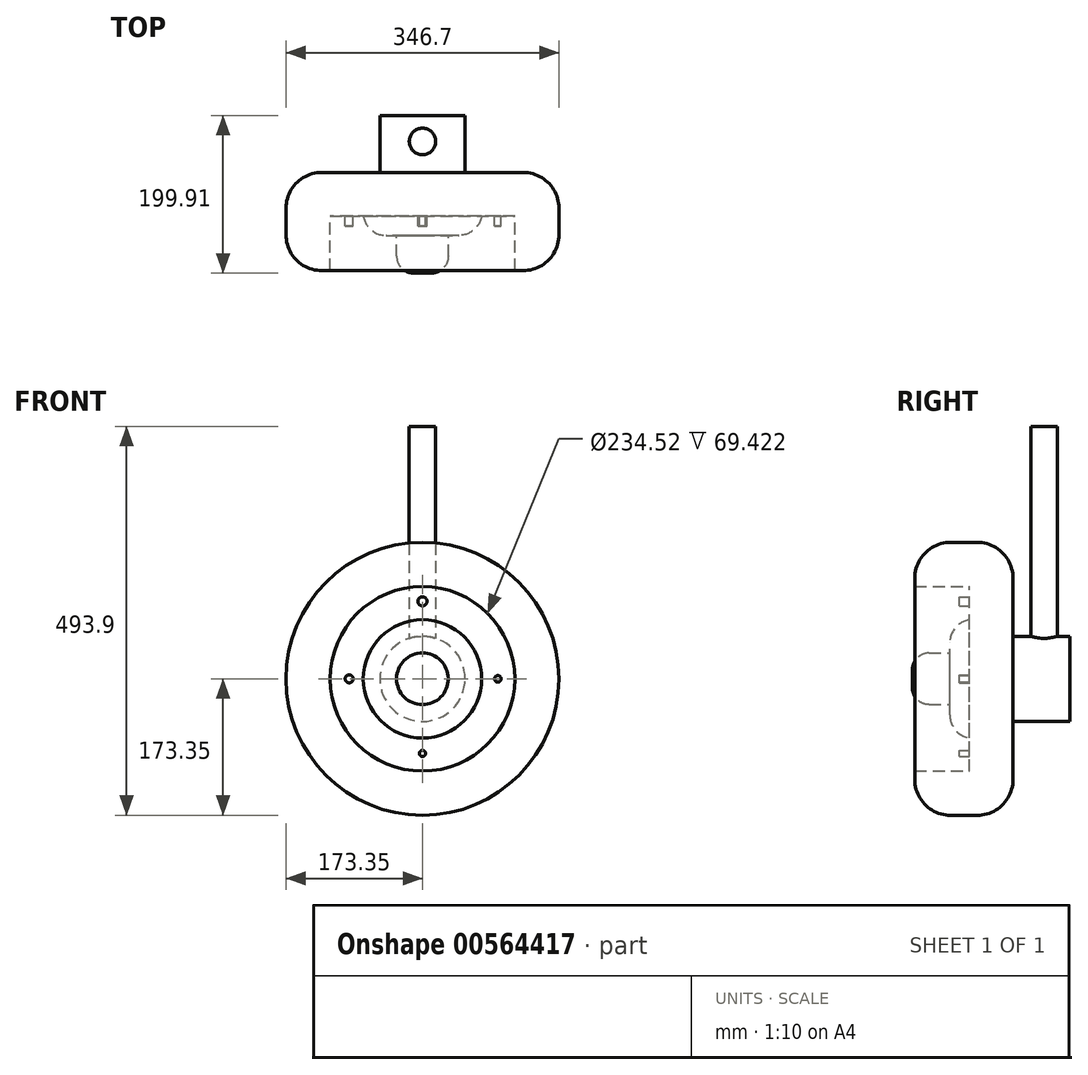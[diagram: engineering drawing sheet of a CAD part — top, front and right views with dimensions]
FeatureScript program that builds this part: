
annotation { "Feature Type Name" : "Feature", "Feature Type Description" : "" }
export const myFeature = defineFeature(function(context is Context, id is Id, definition is map)
    precondition{}
    {
        {
            var Q0;
            Q0=qCreatedBy(makeId("Front.planeOp"),FACE);
            var sketch = newSketch(context, id + "F0", { "sketchPlane" : qUnion([Q0])});
            skCircle(sketch, "E0", {"center": v(0, 0) * mm, "radius": 173.35 * mm});
            skCircle(sketch, "E1", {"center": v(0, 0) * mm, "radius": 117.26 * mm});
            skCircle(sketch, "E2", {"center": v(0, 0) * mm, "radius": 25.29 * mm});
            skSolve(sketch);
        }
        {
            var Q0;
            Q0=makeQuery(id+"F0.imprint","IMPRINT",FACE,{"disambiguationData":[TD([[makeQuery(id+"F0.imprint","IMPRINT",EDGE,{"derivedFrom":sQuery(id+"F0.wireOp",EDGE,"E0")}),1.0]])]});
            extrude(context, id + "F1", {"entities" : qUnion([Q0]), "depth" : 124.69 * mm, "offsetDistance" : 25.4 * mm});
        }
        {
            var Q0;
            Q0=makeQuery(id+"F1.opExtrude","CAP_EDGE",EDGE,{"disambiguationData":[OSD([sQuery(id+"F0.wireOp",EDGE,"E0")])],"isStart":true});
            var Q1;
            Q1=makeQuery(id+"F1.opExtrude","CAP_EDGE",EDGE,{"disambiguationData":[OSD([sQuery(id+"F0.wireOp",EDGE,"E0")])],"isStart":false});
            fillet(context, id + "F2", {"entities" : qUnion([Q0, Q1]), "radius" : 45.43 * mm, "tangentPropagation" : true, "allowEdgeOverflow" : false});
        }
        {
            var Q0;
            Q0=qCreatedBy(makeId("Front.planeOp"),FACE);
            var sketch = newSketch(context, id + "F3", { "sketchPlane" : qUnion([Q0])});
            skCircle(sketch, "E3", {"center": v(0, 0) * mm, "radius": 121.25 * mm});
            skSolve(sketch);
        }
        {
            var Q0;
            Q0 = qSketchRegion(id + "F3", true);
            extrude(context, id + "F4", {"entities" : qUnion([Q0]), "operationType" : NewBodyOperationType.ADD, "depth" : 55.27 * mm, "offsetDistance" : 25.4 * mm});
        }
        {
            var Q0;
            Q0=qCreatedBy(makeId("Front.planeOp"),FACE);
            var sketch = newSketch(context, id + "F5", { "sketchPlane" : qUnion([Q0])});
            skCircle(sketch, "E4", {"center": v(0, 0) * mm, "radius": 75.17 * mm});
            skSolve(sketch);
        }
        {
            var Q0;
            Q0 = qSketchRegion(id + "F5", true);
            extrude(context, id + "F6", {"entities" : qUnion([Q0]), "operationType" : NewBodyOperationType.ADD, "depth" : 80.07 * mm, "offsetDistance" : 25.4 * mm});
        }
        {
            var Q0;
            Q0=qCreatedBy(makeId("Front.planeOp"),FACE);
            var sketch = newSketch(context, id + "F7", { "sketchPlane" : qUnion([Q0])});
            skCircle(sketch, "E5", {"center": v(0, 0) * mm, "radius": 32.78 * mm});
            skSolve(sketch);
        }
        {
            var Q0;
            Q0 = qSketchRegion(id + "F7", true);
            extrude(context, id + "F8", {"entities" : qUnion([Q0]), "operationType" : NewBodyOperationType.ADD, "depth" : 127.76 * mm, "offsetDistance" : 25.4 * mm});
        }
        {
            var Q0;
            Q0=makeQuery(id+"F8.opExtrude","CAP_EDGE",EDGE,{"disambiguationData":[OSD([sQuery(id+"F7.wireOp",EDGE,"E5")])],"isStart":false});
            fillet(context, id + "F9", {"entities" : qUnion([Q0]), "radius" : 21.22 * mm, "tangentPropagation" : true, "allowEdgeOverflow" : false});
        }
        {
            var Q0;
            Q0=makeQuery(id+"F6.opExtrude","CAP_EDGE",EDGE,{"disambiguationData":[OSD([sQuery(id+"F5.wireOp",EDGE,"E4")])],"isStart":false});
            fillet(context, id + "F10", {"entities" : qUnion([Q0]), "radius" : 29.41 * mm, "tangentPropagation" : true, "allowEdgeOverflow" : false});
        }
        {
            var Q0;
            Q0=qCreatedBy(makeId("Front.planeOp"),FACE);
            var sketch = newSketch(context, id + "F11", { "sketchPlane" : qUnion([Q0])});
            skCircle(sketch, "E6", {"center": v(0, 0) * mm, "radius": 54.14 * mm});
            skSolve(sketch);
        }
        {
            var Q0;
            Q0 = qSketchRegion(id + "F11", true);
            extrude(context, id + "F12", {"entities" : qUnion([Q0]), "operationType" : NewBodyOperationType.ADD, "oppositeDirection" : true, "depth" : 72.15 * mm, "offsetDistance" : 25.4 * mm});
        }
        {
            var Q0;
            Q0=qCreatedBy(makeId("Top.planeOp"),FACE);
            var sketch = newSketch(context, id + "F13", { "sketchPlane" : qUnion([Q0])});
            skCircle(sketch, "E7", {"center": v(0, 39.34) * mm, "radius": 16.79 * mm});
            skSolve(sketch);
        }
        {
            var Q0;
            Q0 = qSketchRegion(id + "F13", true);
            extrude(context, id + "F14", {"entities" : qUnion([Q0]), "operationType" : NewBodyOperationType.ADD, "depth" : 320.55 * mm, "offsetDistance" : 25.4 * mm});
        }
        {
            var Q0;
            Q0=qCreatedBy(makeId("Front.planeOp"),FACE);
            var sketch = newSketch(context, id + "F15", { "sketchPlane" : qUnion([Q0])});
            skCircle(sketch, "E8", {"center": v(0, 98.5) * mm, "radius": 5.77 * mm});
            skCircle(sketch, "E9", {"center": v(-93.1, 0) * mm, "radius": 5.06 * mm});
            skCircle(sketch, "E10", {"center": v(0, -94.77) * mm, "radius": 3.9 * mm});
            skCircle(sketch, "E11", {"center": v(95.73, 0) * mm, "radius": 4.17 * mm});
            skSolve(sketch);
        }
        {
            var Q0;
            Q0 = qSketchRegion(id + "F15", true);
            extrude(context, id + "F16", {"entities" : qUnion([Q0]), "operationType" : NewBodyOperationType.ADD, "depth" : 68.34 * mm, "offsetDistance" : 25.4 * mm});
        }
    });
